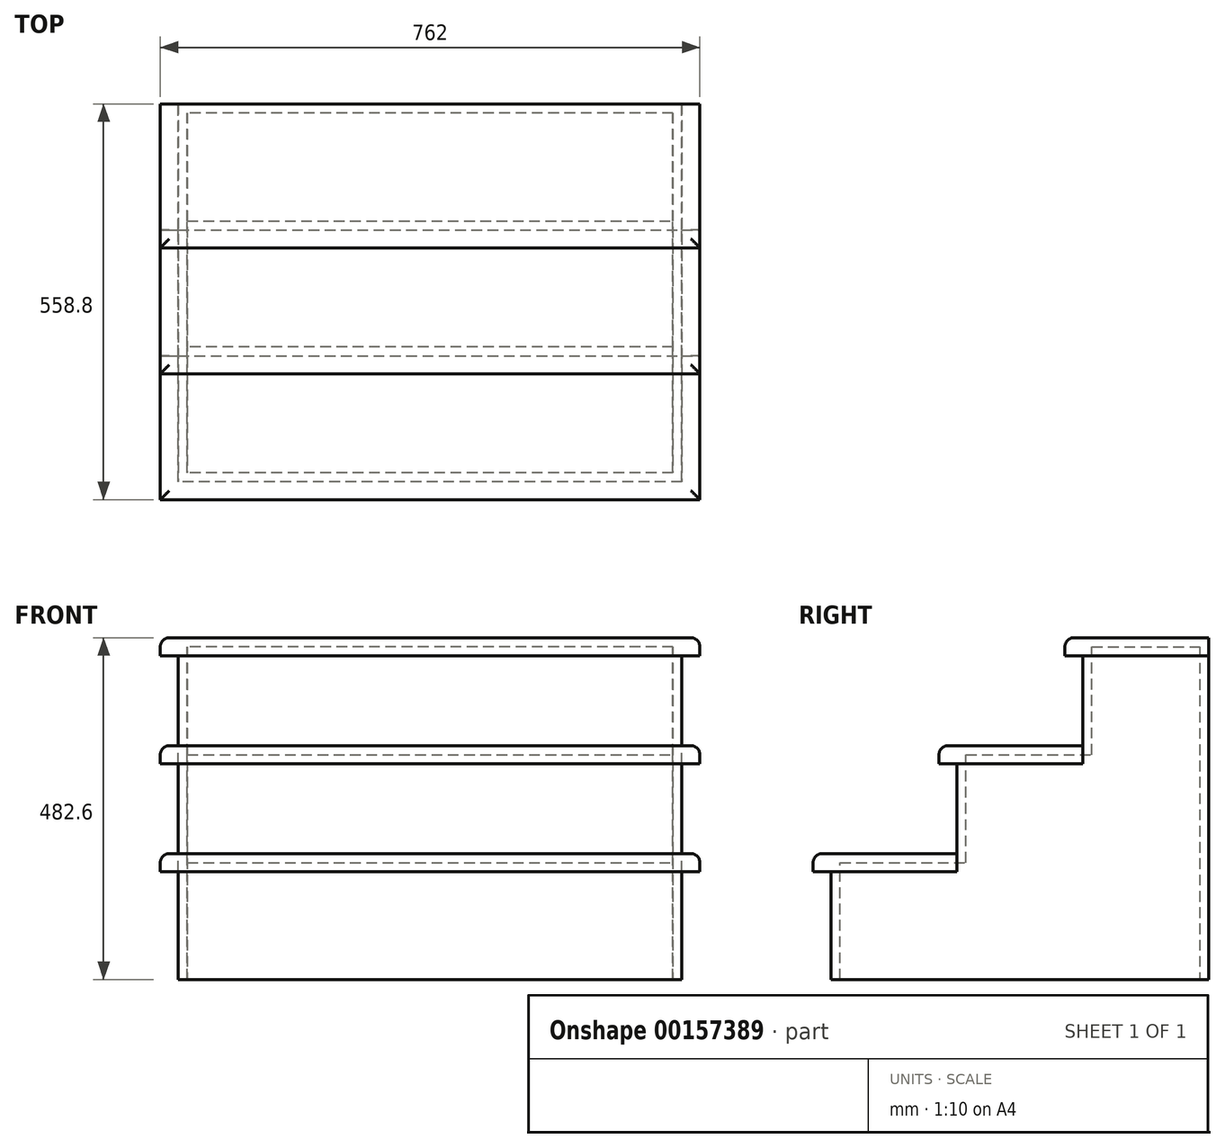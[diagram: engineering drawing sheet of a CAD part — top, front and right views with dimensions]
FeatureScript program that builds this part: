
annotation { "Feature Type Name" : "Feature", "Feature Type Description" : "" }
export const myFeature = defineFeature(function(context is Context, id is Id, definition is map)
    precondition{}
    {
        {
            var Q0;
            Q0=qCreatedBy(makeId("Right.planeOp"),FACE);
            var sketch = newSketch(context, id + "F0", { "sketchPlane" : qUnion([Q0])});
            skLineSegment(sketch, "E0", {"start": v(0, 0) * mm, "end": v(-533.4, 0) * mm});
            skLineSegment(sketch, "E1", {"start": v(-533.4, 0) * mm, "end": v(-533.4, 152.4) * mm});
            skLineSegment(sketch, "E2", {"start": v(-533.4, 152.4) * mm, "end": v(-355.6, 152.4) * mm});
            skLineSegment(sketch, "E3", {"start": v(-355.6, 152.4) * mm, "end": v(-355.6, 304.8) * mm});
            skLineSegment(sketch, "E4", {"start": v(-355.6, 304.8) * mm, "end": v(-177.8, 304.8) * mm});
            skLineSegment(sketch, "E5", {"start": v(-177.8, 304.8) * mm, "end": v(-177.8, 457.2) * mm});
            skLineSegment(sketch, "E6", {"start": v(-177.8, 457.2) * mm, "end": v(0, 457.2) * mm});
            skLineSegment(sketch, "E7", {"start": v(0, 457.2) * mm, "end": v(0, 0) * mm});
            skSolve(sketch);
        }
        {
            var Q0;
            Q0 = qSketchRegion(id + "F0", true);
            extrude(context, id + "F1", {"entities" : qUnion([Q0]), "depth" : 711.2 * mm});
        }
        {
            var Q0;
            Q0=makeQuery(id+"F1.opExtrude","SWEPT_FACE",FACE,{"disambiguationData":[OSD([sQuery(id+"F0.wireOp",EDGE,"E5")])]});
            var sketch = newSketch(context, id + "F2", { "sketchPlane" : qUnion([Q0])});
            skLineSegment(sketch, "E8.bottom", {"start": v(-25.4, 304.8) * mm, "end": v(736.6, 304.8) * mm});
            skLineSegment(sketch, "E8.top", {"start": v(-25.4, 330.2) * mm, "end": v(736.6, 330.2) * mm});
            skLineSegment(sketch, "E8.left", {"start": v(-25.4, 304.8) * mm, "end": v(-25.4, 330.2) * mm});
            skLineSegment(sketch, "E8.right", {"start": v(736.6, 304.8) * mm, "end": v(736.6, 330.2) * mm});
            skSolve(sketch);
        }
        {
            var Q0;
            Q0 = qSketchRegion(id + "F2", true);
            extrude(context, id + "F3", {"entities" : qUnion([Q0]), "operationType" : NewBodyOperationType.ADD, "depth" : 203.2 * mm});
        }
        {
            var Q0;
            Q0=makeQuery(id+"F1.opExtrude","SWEPT_FACE",FACE,{"disambiguationData":[OSD([sQuery(id+"F0.wireOp",EDGE,"E7")])]});
            var sketch = newSketch(context, id + "F4", { "sketchPlane" : qUnion([Q0])});
            skLineSegment(sketch, "E9.bottom", {"start": v(-736.6, 457.2) * mm, "end": v(25.4, 457.2) * mm});
            skLineSegment(sketch, "E9.top", {"start": v(-736.6, 482.6) * mm, "end": v(25.4, 482.6) * mm});
            skLineSegment(sketch, "E9.left", {"start": v(-736.6, 457.2) * mm, "end": v(-736.6, 482.6) * mm});
            skLineSegment(sketch, "E9.right", {"start": v(25.4, 457.2) * mm, "end": v(25.4, 482.6) * mm});
            skSolve(sketch);
        }
        {
            var Q0;
            Q0 = qSketchRegion(id + "F4", true);
            extrude(context, id + "F5", {"entities" : qUnion([Q0]), "operationType" : NewBodyOperationType.ADD, "oppositeDirection" : true, "depth" : 203.2 * mm});
        }
        {
            var Q0;
            Q0=makeQuery(id+"F1.opExtrude","SWEPT_FACE",FACE,{"disambiguationData":[OSD([sQuery(id+"F0.wireOp",EDGE,"E3")])]});
            var sketch = newSketch(context, id + "F6", { "sketchPlane" : qUnion([Q0])});
            skLineSegment(sketch, "E10.bottom", {"start": v(-25.4, 152.4) * mm, "end": v(736.6, 152.4) * mm});
            skLineSegment(sketch, "E10.top", {"start": v(-25.4, 177.8) * mm, "end": v(736.6, 177.8) * mm});
            skLineSegment(sketch, "E10.left", {"start": v(-25.4, 152.4) * mm, "end": v(-25.4, 177.8) * mm});
            skLineSegment(sketch, "E10.right", {"start": v(736.6, 152.4) * mm, "end": v(736.6, 177.8) * mm});
            skSolve(sketch);
        }
        {
            var Q0;
            Q0 = qSketchRegion(id + "F6", true);
            extrude(context, id + "F7", {"entities" : qUnion([Q0]), "operationType" : NewBodyOperationType.ADD, "depth" : 203.2 * mm});
        }
        {
            var Q0;
            Q0=makeQuery(id+"F5.opExtrude","SWEPT_EDGE",EDGE,{"disambiguationData":[OSD([sQuery(id+"F4.wireOp",EDGE,"E9.top"),sQuery(id+"F4.wireOp",EDGE,"E9.right")])]});
            var Q1;
            Q1=makeQuery(id+"F5.opExtrude","CAP_EDGE",EDGE,{"disambiguationData":[OSD([sQuery(id+"F4.wireOp",EDGE,"E9.top")])],"isStart":false});
            var Q2;
            Q2=makeQuery(id+"F5.opExtrude","SWEPT_EDGE",EDGE,{"disambiguationData":[OSD([sQuery(id+"F4.wireOp",EDGE,"E9.top"),sQuery(id+"F4.wireOp",EDGE,"E9.left")])]});
            var Q3;
            Q3=makeQuery(id+"F3.opExtrude","SWEPT_EDGE",EDGE,{"disambiguationData":[OSD([sQuery(id+"F2.wireOp",EDGE,"E8.top"),sQuery(id+"F2.wireOp",EDGE,"E8.left")])]});
            var Q4;
            Q4=makeQuery(id+"F3.opExtrude","CAP_EDGE",EDGE,{"disambiguationData":[OSD([sQuery(id+"F2.wireOp",EDGE,"E8.top")])],"isStart":false});
            var Q5;
            Q5=makeQuery(id+"F3.opExtrude","SWEPT_EDGE",EDGE,{"disambiguationData":[OSD([sQuery(id+"F2.wireOp",EDGE,"E8.top"),sQuery(id+"F2.wireOp",EDGE,"E8.right")])]});
            var Q6;
            Q6=makeQuery(id+"F7.opExtrude","SWEPT_EDGE",EDGE,{"disambiguationData":[OSD([sQuery(id+"F6.wireOp",EDGE,"E10.top"),sQuery(id+"F6.wireOp",EDGE,"E10.left")])]});
            var Q7;
            Q7=makeQuery(id+"F7.opExtrude","CAP_EDGE",EDGE,{"disambiguationData":[OSD([sQuery(id+"F6.wireOp",EDGE,"E10.top")])],"isStart":false});
            var Q8;
            Q8=makeQuery(id+"F7.opExtrude","SWEPT_EDGE",EDGE,{"disambiguationData":[OSD([sQuery(id+"F6.wireOp",EDGE,"E10.top"),sQuery(id+"F6.wireOp",EDGE,"E10.right")])]});
            fillet(context, id + "F8", {"entities" : qUnion([Q0, Q1, Q2, Q3, Q4, Q5, Q6, Q7, Q8]), "radius" : 12.7 * mm, "tangentPropagation" : true, "allowEdgeOverflow" : false});
        }
        {
            var Q0;
            Q0=makeQuery(id+"F1.opExtrude","SWEPT_FACE",FACE,{"disambiguationData":[OSD([sQuery(id+"F0.wireOp",EDGE,"E0")])]});
            shell(context, id + "F9", {"entities" : qUnion([Q0]), "thickness" : 12.7 * mm});
        }
    });
